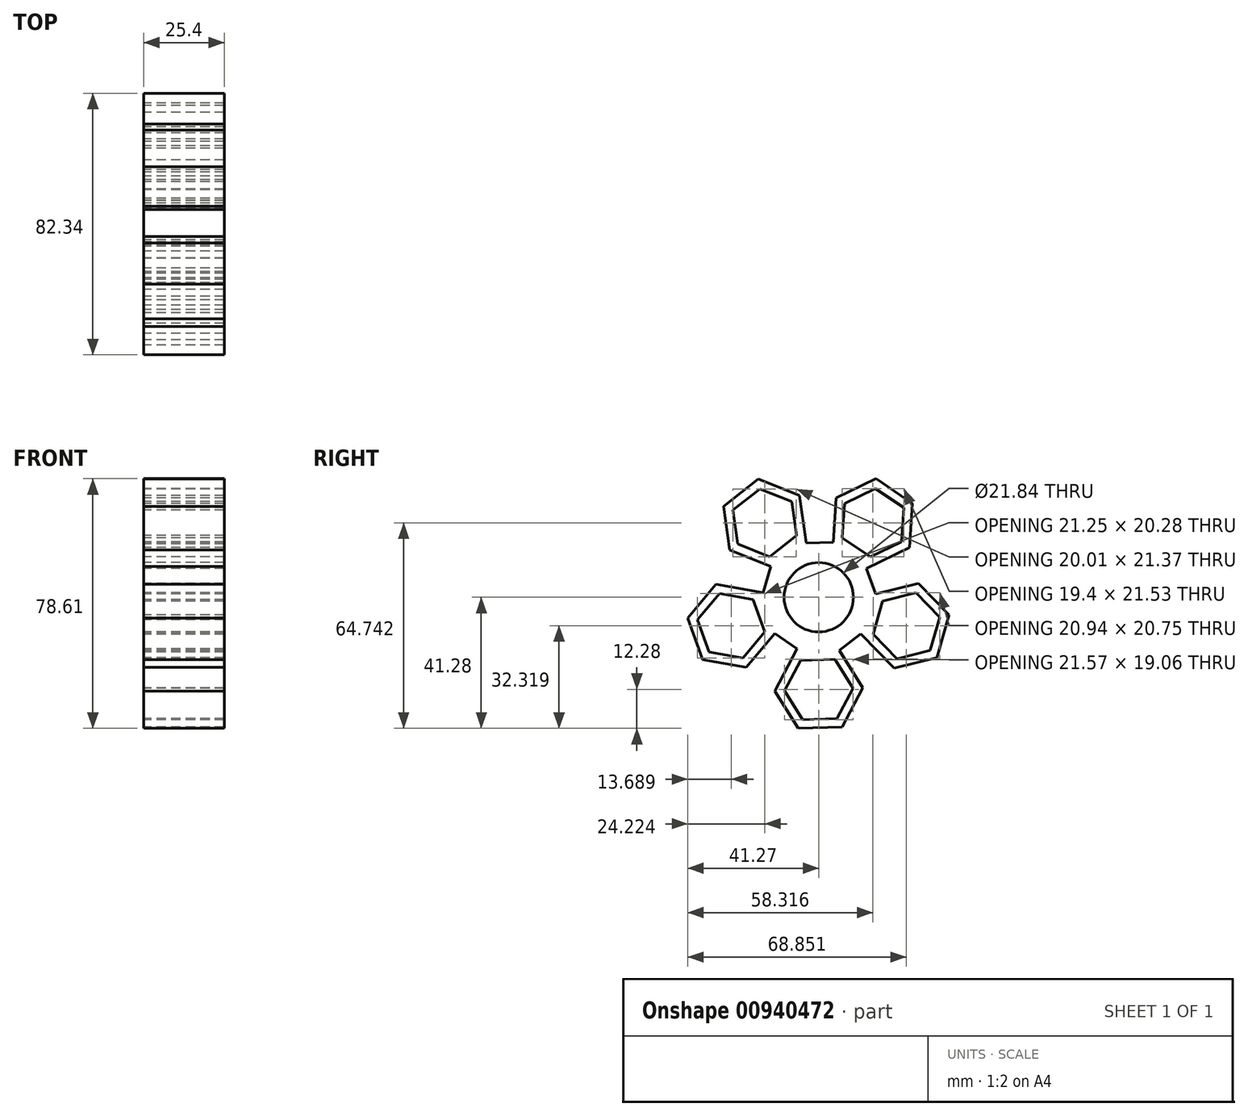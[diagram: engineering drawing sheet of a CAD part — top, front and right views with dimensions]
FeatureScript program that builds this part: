
annotation { "Feature Type Name" : "Feature", "Feature Type Description" : "" }
export const myFeature = defineFeature(function(context is Context, id is Id, definition is map)
    precondition{}
    {
        {
            var Q0;
            Q0=qCreatedBy(makeId("Right.planeOp"),FACE);
            var sketch = newSketch(context, id + "F0", { "sketchPlane" : qUnion([Q0])});
            skCircle(sketch, "E0.cCircle", {"center": v(0, -29) * mm, "radius": 9.35 * mm, "construction": true});
            skLineSegment(sketch, "E0.0", {"start": v(10.78, -28.62) * mm, "end": v(5.72, -38.15) * mm});
            skLineSegment(sketch, "E0.1", {"start": v(5.72, -38.15) * mm, "end": v(-5.06, -38.53) * mm});
            skLineSegment(sketch, "E0.2", {"start": v(-5.06, -38.53) * mm, "end": v(-10.78, -29.38) * mm});
            skLineSegment(sketch, "E0.3", {"start": v(-10.78, -29.38) * mm, "end": v(-5.72, -19.85) * mm});
            skLineSegment(sketch, "E0.4", {"start": v(-5.72, -19.85) * mm, "end": v(5.06, -19.47) * mm});
            skLineSegment(sketch, "E0.5", {"start": v(5.06, -19.47) * mm, "end": v(10.78, -28.62) * mm});
            skPoint(sketch, "E0.0.midPoint", {"position": v(8.25, -33.39) * mm});
            skCircle(sketch, "E1", {"center": v(0, 0) * mm, "radius": 10.92 * mm});
            skLineSegment(sketch, "E2.1.0", {"start": v(17.11, -11.57) * mm, "end": v(20.08, -1.2) * mm});
            skPoint(sketch, "E2.1.1", {"position": v(34.3, -2.47) * mm});
            skLineSegment(sketch, "E2.1.2", {"start": v(35.08, -16.72) * mm, "end": v(24.6, -19.33) * mm});
            skLineSegment(sketch, "E2.1.3", {"start": v(38.05, -6.35) * mm, "end": v(35.08, -16.72) * mm});
            skLineSegment(sketch, "E2.1.4", {"start": v(30.55, 1.41) * mm, "end": v(38.05, -6.35) * mm});
            skCircle(sketch, "E2.1.5", {"center": v(27.58, -8.96) * mm, "radius": 9.35 * mm, "construction": true});
            skLineSegment(sketch, "E2.1.6", {"start": v(24.6, -19.33) * mm, "end": v(17.11, -11.57) * mm});
            skLineSegment(sketch, "E2.1.7", {"start": v(20.08, -1.2) * mm, "end": v(30.55, 1.41) * mm});
            skLineSegment(sketch, "E2.2.0", {"start": v(16.3, 12.7) * mm, "end": v(7.35, 18.73) * mm});
            skPoint(sketch, "E2.2.1", {"position": v(12.95, 31.86) * mm});
            skLineSegment(sketch, "E2.2.2", {"start": v(26.74, 28.2) * mm, "end": v(26, 17.43) * mm});
            skLineSegment(sketch, "E2.2.3", {"start": v(17.8, 34.23) * mm, "end": v(26.74, 28.2) * mm});
            skLineSegment(sketch, "E2.2.4", {"start": v(8.1, 29.5) * mm, "end": v(17.8, 34.23) * mm});
            skCircle(sketch, "E2.2.5", {"center": v(17.05, 23.46) * mm, "radius": 9.35 * mm, "construction": true});
            skLineSegment(sketch, "E2.2.6", {"start": v(26, 17.43) * mm, "end": v(16.3, 12.7) * mm});
            skLineSegment(sketch, "E2.2.7", {"start": v(7.35, 18.73) * mm, "end": v(8.1, 29.5) * mm});
            skLineSegment(sketch, "E2.3.0", {"start": v(-7.04, 19.42) * mm, "end": v(-15.54, 12.78) * mm});
            skPoint(sketch, "E2.3.1", {"position": v(-26.3, 22.16) * mm});
            skLineSegment(sketch, "E2.3.2", {"start": v(-18.55, 34.15) * mm, "end": v(-8.54, 30.1) * mm});
            skLineSegment(sketch, "E2.3.3", {"start": v(-27.05, 27.5) * mm, "end": v(-18.55, 34.15) * mm});
            skLineSegment(sketch, "E2.3.4", {"start": v(-25.55, 16.82) * mm, "end": v(-27.05, 27.5) * mm});
            skCircle(sketch, "E2.3.5", {"center": v(-17.05, 23.46) * mm, "radius": 9.35 * mm, "construction": true});
            skLineSegment(sketch, "E2.3.6", {"start": v(-8.54, 30.1) * mm, "end": v(-7.04, 19.42) * mm});
            skLineSegment(sketch, "E2.3.7", {"start": v(-15.54, 12.78) * mm, "end": v(-25.55, 16.82) * mm});
            skLineSegment(sketch, "E2.4.0", {"start": v(-20.65, -0.7) * mm, "end": v(-16.95, -10.83) * mm});
            skPoint(sketch, "E2.4.1", {"position": v(-29.2, -18.16) * mm});
            skLineSegment(sketch, "E2.4.2", {"start": v(-38.2, -7.09) * mm, "end": v(-31.27, 1.18) * mm});
            skLineSegment(sketch, "E2.4.3", {"start": v(-34.52, -17.23) * mm, "end": v(-38.2, -7.09) * mm});
            skLineSegment(sketch, "E2.4.4", {"start": v(-23.89, -19.1) * mm, "end": v(-34.52, -17.23) * mm});
            skCircle(sketch, "E2.4.5", {"center": v(-27.58, -8.96) * mm, "radius": 9.35 * mm, "construction": true});
            skLineSegment(sketch, "E2.4.6", {"start": v(-31.27, 1.18) * mm, "end": v(-20.65, -0.7) * mm});
            skLineSegment(sketch, "E2.4.7", {"start": v(-16.95, -10.83) * mm, "end": v(-23.89, -19.1) * mm});
            skLineSegment(sketch, "E3.0", {"start": v(18.01, 37.33) * mm, "end": v(29.54, 29.56) * mm});
            skLineSegment(sketch, "E3.1", {"start": v(29.54, 29.56) * mm, "end": v(28.57, 15.69) * mm});
            skLineSegment(sketch, "E3.2", {"start": v(28.57, 15.69) * mm, "end": v(16.08, 9.6) * mm});
            skLineSegment(sketch, "E3.4", {"start": v(4.55, 17.36) * mm, "end": v(5.52, 31.23) * mm});
            skLineSegment(sketch, "E3.5", {"start": v(5.52, 31.23) * mm, "end": v(18.01, 37.33) * mm});
            skPoint(sketch, "E3.0.midPoint", {"position": v(23.78, 33.44) * mm});
            skLineSegment(sketch, "E4.1.0", {"start": v(-29.94, 28.67) * mm, "end": v(-18.98, 37.23) * mm});
            skLineSegment(sketch, "E4.1.1", {"start": v(-18.98, 37.23) * mm, "end": v(-6.1, 32.02) * mm});
            skLineSegment(sketch, "E4.1.2", {"start": v(-6.1, 32.02) * mm, "end": v(-4.15, 18.26) * mm});
            skLineSegment(sketch, "E4.1.4", {"start": v(-15.1, 9.7) * mm, "end": v(-28, 14.9) * mm});
            skLineSegment(sketch, "E4.1.5", {"start": v(-28, 14.9) * mm, "end": v(-29.94, 28.67) * mm});
            skLineSegment(sketch, "E4.2.0", {"start": v(-36.52, -19.61) * mm, "end": v(-41.27, -6.55) * mm});
            skLineSegment(sketch, "E4.2.1", {"start": v(-41.27, -6.55) * mm, "end": v(-32.34, 4.1) * mm});
            skLineSegment(sketch, "E4.2.2", {"start": v(-32.34, 4.1) * mm, "end": v(-18.65, 1.7) * mm});
            skLineSegment(sketch, "E4.2.4", {"start": v(-13.89, -11.37) * mm, "end": v(-22.82, -22.03) * mm});
            skLineSegment(sketch, "E4.2.5", {"start": v(-22.82, -22.03) * mm, "end": v(-36.52, -19.61) * mm});
            skLineSegment(sketch, "E4.3.0", {"start": v(7.37, -40.79) * mm, "end": v(-6.53, -41.28) * mm});
            skLineSegment(sketch, "E4.3.1", {"start": v(-6.53, -41.28) * mm, "end": v(-13.9, -29.49) * mm});
            skLineSegment(sketch, "E4.3.2", {"start": v(-13.9, -29.49) * mm, "end": v(-7.37, -17.21) * mm});
            skLineSegment(sketch, "E4.3.4", {"start": v(6.53, -16.72) * mm, "end": v(13.9, -28.51) * mm});
            skLineSegment(sketch, "E4.3.5", {"start": v(13.9, -28.51) * mm, "end": v(7.37, -40.79) * mm});
            skLineSegment(sketch, "E4.4.0", {"start": v(41.07, -5.6) * mm, "end": v(37.24, -18.96) * mm});
            skLineSegment(sketch, "E4.4.1", {"start": v(37.24, -18.96) * mm, "end": v(23.75, -22.33) * mm});
            skLineSegment(sketch, "E4.4.2", {"start": v(23.75, -22.33) * mm, "end": v(14.1, -12.33) * mm});
            skLineSegment(sketch, "E4.4.4", {"start": v(17.92, 1.04) * mm, "end": v(31.41, 4.4) * mm});
            skLineSegment(sketch, "E4.4.5", {"start": v(31.41, 4.4) * mm, "end": v(41.07, -5.6) * mm});
            skLineSegment(sketch, "E5", {"start": v(-4.15, 18.26) * mm, "end": v(-3.99, 17.07) * mm});
            skLineSegment(sketch, "E6.1.0", {"start": v(-18.65, 1.7) * mm, "end": v(-17.46, 1.48) * mm});
            skLineSegment(sketch, "E6.2.0", {"start": v(-7.37, -17.21) * mm, "end": v(-6.8, -16.15) * mm});
            skLineSegment(sketch, "E6.3.0", {"start": v(14.1, -12.33) * mm, "end": v(13.26, -11.46) * mm});
            skLineSegment(sketch, "E6.4.0", {"start": v(16.08, 9.6) * mm, "end": v(15, 9.06) * mm});
            skLineSegment(sketch, "E7", {"start": v(4.55, 17.36) * mm, "end": v(-3.99, 17.07) * mm});
            skLineSegment(sketch, "E8.1.0", {"start": v(-15.1, 9.7) * mm, "end": v(-17.46, 1.48) * mm});
            skLineSegment(sketch, "E8.2.0", {"start": v(-13.89, -11.37) * mm, "end": v(-6.8, -16.15) * mm});
            skLineSegment(sketch, "E8.3.0", {"start": v(6.53, -16.72) * mm, "end": v(13.26, -11.46) * mm});
            skLineSegment(sketch, "E8.4.0", {"start": v(17.92, 1.04) * mm, "end": v(15, 9.06) * mm});
            skSolve(sketch);
        }
        {
            var Q0;
            Q0 = qSketchRegion(id + "F0", true);
            extrude(context, id + "F1", {"entities" : qUnion([Q0]), "depth" : 25.4 * mm, "offsetDistance" : 25.4 * mm});
        }
        {
            var Q0;
            Q0 = qSketchRegion(id + "F0", true);
            extrude(context, id + "F2", {"entities" : qUnion([Q0]), "operationType" : NewBodyOperationType.ADD, "depth" : 25 * mm, "offsetDistance" : 25 * mm});
        }
    });
